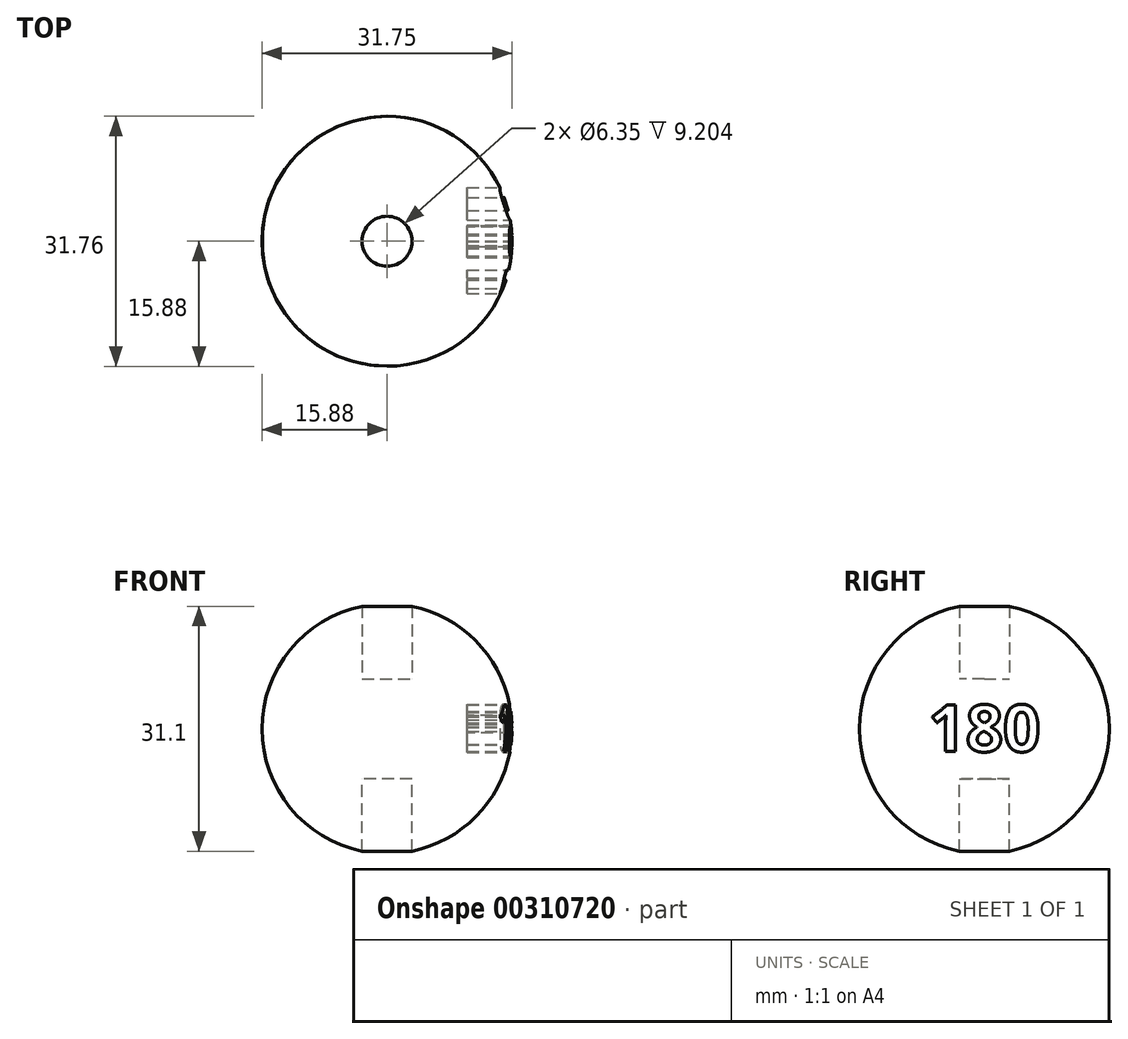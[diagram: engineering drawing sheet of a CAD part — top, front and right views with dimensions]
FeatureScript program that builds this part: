
annotation { "Feature Type Name" : "Feature", "Feature Type Description" : "" }
export const myFeature = defineFeature(function(context is Context, id is Id, definition is map)
    precondition{}
    {
        {
            var Q0;
            Q0=qCreatedBy(makeId("Front.planeOp"),FACE);
            var sketch = newSketch(context, id + "F0", { "sketchPlane" : qUnion([Q0])});
            skCircle(sketch, "E0", {"center": v(0, 0) * mm, "radius": 15.88 * mm});
            skSolve(sketch);
        }
        {
            var Q0;
            Q0=qCreatedBy(makeId("Top.planeOp"),FACE);
            var sketch = newSketch(context, id + "F1", { "sketchPlane" : qUnion([Q0])});
            skArc(sketch, "E1", {"start": v(0, 15.88) * mm, "mid": v(-15.88, 0) * mm, "end": v(0, -15.88) * mm});
            skLineSegment(sketch, "E2", {"start": v(0, 15.88) * mm, "end": v(0, -15.88) * mm});
            skSolve(sketch);
        }
        {
            var Q0;
            Q0=makeQuery(id+"F1.imprint","IMPRINT",FACE,{"disambiguationData":[TD([[makeQuery(id+"F1.imprint","IMPRINT",EDGE,{"derivedFrom":sQuery(id+"F1.wireOp",EDGE,"E1")}),1.0]])]});
            var Q1;
            Q1=sQuery(id+"F0.wireOp",EDGE,"E0");
            revolve(context, id + "F2", {"entities" : qUnion([Q0]), "axis" : qUnion([Q1]), "revolveType" : RevolveType.FULL});
        }
        {
            var Q0;
            Q0=qCreatedBy(makeId("Top.planeOp"),FACE);
            cPlane(context, id + "F3", {"entities" : qUnion([Q0]), "cplaneType" : CPlaneType.OFFSET, "offset" : 6.35 * mm, "width" : 152.4 * mm, "height" : 152.4 * mm});
        }
        {
            var Q0;
            Q0=qCreatedBy(id+"F3.planeOp",FACE);
            var sketch = newSketch(context, id + "F4", { "sketchPlane" : qUnion([Q0])});
            skCircle(sketch, "E3", {"center": v(0, 0) * mm, "radius": 3.18 * mm});
            skSolve(sketch);
        }
        {
            var Q0;
            Q0=makeQuery(id+"F4.imprint","IMPRINT",FACE,{"disambiguationData":[TD([[makeQuery(id+"F4.imprint","IMPRINT",EDGE,{"derivedFrom":sQuery(id+"F4.wireOp",EDGE,"E3")}),1.0]])]});
            extrude(context, id + "F5", {"entities" : qUnion([Q0]), "depth" : 25.4 * mm});
        }
        {
            var Q0;
            Q0=qCreatedBy(makeId("Top.planeOp"),FACE);
            cPlane(context, id + "F6", {"entities" : qUnion([Q0]), "cplaneType" : CPlaneType.OFFSET, "offset" : 6.35 * mm, "oppositeDirection" : true, "width" : 152.4 * mm, "height" : 152.4 * mm});
        }
        {
            var Q0;
            Q0=qCreatedBy(id+"F6.planeOp",FACE);
            var sketch = newSketch(context, id + "F7", { "sketchPlane" : qUnion([Q0])});
            skCircle(sketch, "E4", {"center": v(0, 0) * mm, "radius": 3.18 * mm});
            skSolve(sketch);
        }
        {
            var Q0;
            Q0=makeQuery(id+"F7.imprint","IMPRINT",FACE,{"disambiguationData":[TD([[makeQuery(id+"F7.imprint","IMPRINT",EDGE,{"derivedFrom":sQuery(id+"F7.wireOp",EDGE,"E4")}),1.0]])]});
            var Q1;
            Q1=makeQuery(id+"F5.opExtrude","CAP_FACE",FACE,{"disambiguationData":[OSD([sQuery(id+"F4.wireOp",EDGE,"E3")])],"isStart":false});
            extrude(context, id + "F8", {"entities" : qUnion([Q0, Q1]), "oppositeDirection" : true, "depth" : 25.4 * mm});
        }
        {
            var Q0;
            Q0=makeQuery(id+"F8.opExtrude","SWEPT_BODY",BODY,{"disambiguationData":[OSD([sQuery(id+"F4.wireOp",EDGE,"E3")])]});
            deleteBodies(context, id + "F9", {"entities" : qUnion([Q0])});
        }
        {
            var Q0;
            Q0=makeQuery(id+"F5.opExtrude","SWEPT_BODY",BODY,{"disambiguationData":[OSD([sQuery(id+"F4.wireOp",EDGE,"E3")])]});
            var Q1;
            Q1=makeQuery(id+"F8.opExtrude","SWEPT_BODY",BODY,{"disambiguationData":[OSD([sQuery(id+"F7.wireOp",EDGE,"E4")])]});
            var Q2;
            Q2=makeQuery(id+"F2.opRevolve","SWEPT_BODY",BODY,{"disambiguationData":[OSD([sQuery(id+"F1.wireOp",EDGE,"E1"),sQuery(id+"F1.wireOp",EDGE,"E2")])]});
            booleanBodies(context, id + "F10", {"operationType" : BooleanOperationType.SUBTRACTION, "tools" : qUnion([Q0, Q1]), "targets" : qUnion([Q2])});
        }
        {
            var Q0;
            Q0=qCreatedBy(makeId("Right.planeOp"),FACE);
            cPlane(context, id + "F11", {"entities" : qUnion([Q0]), "cplaneType" : CPlaneType.OFFSET, "offset" : 16.5 * mm, "width" : 152.4 * mm, "height" : 152.4 * mm});
        }
        {
            var Q0;
            Q0=qCreatedBy(id+"F11.planeOp",FACE);
            var sketch = newSketch(context, id + "F12", { "sketchPlane" : qUnion([Q0])});
            skText(sketch, "E5", { "text": "180", "fontName": "OpenSans-Bold.ttf"});
            const initialGuessF12  = {"E5": [-0.0071, -0.0029, 1, 0, 0.00598]};
            skSetInitialGuess(sketch, initialGuessF12);
            skSolve(sketch);
        }
        {
            var Q0;
            Q0 = qSketchRegion(id + "F12", true);
            extrude(context, id + "F13", {"entities" : qUnion([Q0]), "operationType" : NewBodyOperationType.REMOVE, "oppositeDirection" : true, "depth" : 6.35 * mm});
        }
    });
